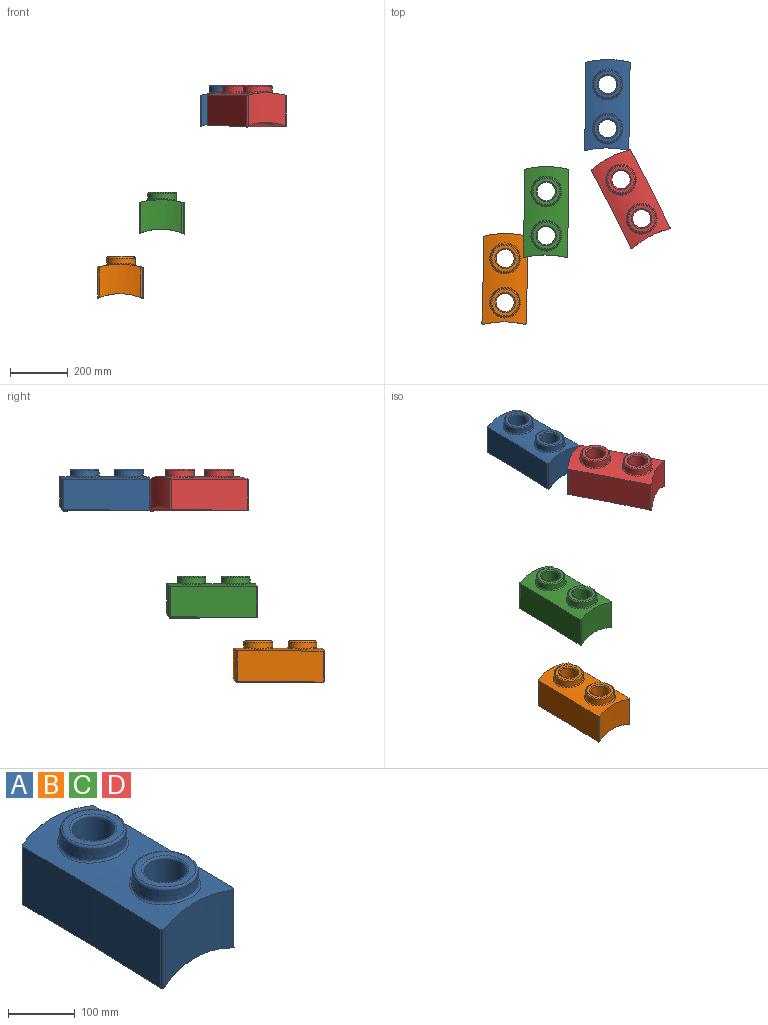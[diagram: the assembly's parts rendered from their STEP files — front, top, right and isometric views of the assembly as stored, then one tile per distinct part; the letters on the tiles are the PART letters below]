
ASSEMBLY  parts=4 mates=1
PART A: 32 faces, bbox 157.2x313.4x143.9 mm
  f0: cylinder r=304.8mm len=313.43mm, axis (0,-1,0), area 29104.2mm2, adj f2,f3,f4,f5,f16,f17,f28,f29
  f1: cylinder r=203.2mm len=313.43mm, axis (0,-1,0), area 28881.3mm2, adj f2,f3,f4,f5,f24,f25,f28,f29
  f2: cylinder r=8000mm len=297.11mm, axis (0,0,-1), area 31878.8mm2, adj f0,f1,f28,f31
  f3: cylinder r=304.8mm len=146.61mm, axis (0,0,-1), area 15275.7mm2, adj f0,f1,f28,f29
  f4: cylinder r=7847.6mm len=296.74mm, axis (0,0,-1), area 31538.3mm2, adj f0,f1,f29,f30
  f5: cylinder r=304.8mm len=143.08mm, axis (0,0,-1), area 14885.5mm2, adj f0,f1,f30,f31
  f6: cone r=50.8mm half-angle=0.5deg, axis (0,0,-1), area 6902.9mm2, adj f25,f26
  f7: plane 94.05x94.05mm, normal (0,0,-1), area 3045mm2, adj f22,f26
  f8: cone r=50.8mm half-angle=0.5deg, axis (0,0,-1), area 6902.9mm2, adj f24,f27
  f9: plane 94.05x94.05mm, normal (0,0,-1), area 3045mm2, adj f23,f27
  f10: cylinder r=31.43mm len=93.98mm, axis (0,0,-1), area 18559.7mm2, adj f21,f23
  f11: cylinder r=31.43mm len=93.98mm, axis (0,0,-1), area 18559.7mm2, adj f18,f22
  f12: cone r=50.8mm half-angle=0.5deg, axis (0,0,-1), area 6296.1mm2, adj f17,f20
  f13: plane 91.39x91.39mm, normal (0,0,1), area 2657.6mm2, adj f20,f21
  f14: cone r=50.8mm half-angle=0.5deg, axis (0,0,-1), area 6296.1mm2, adj f16,f19
  f15: plane 91.39x91.39mm, normal (0,0,1), area 2657.6mm2, adj f18,f19
  f16: bspline ~106.96x105.73mm, area 1802.5mm2, adj f0,f14
  f17: bspline ~106.96x105.73mm, area 1802.5mm2, adj f0,f12
  f18: torus R=35.24mm, axis (0,0,1), area 1234mm2, adj f11,f15
  f19: torus R=45.69mm, axis (0,0,1), area 1799.1mm2, adj f14,f15
  f20: torus R=45.69mm, axis (0,0,1), area 1799.1mm2, adj f12,f13
  f21: torus R=35.24mm, axis (0,0,1), area 1234mm2, adj f10,f13
  f22: torus R=35.24mm, axis (0,0,1), area 1234mm2, adj f7,f11
  f23: torus R=35.24mm, axis (0,0,1), area 1234mm2, adj f9,f10
  f24: bspline ~109.63x107.73mm, area 1793.9mm2, adj f1,f8
  f25: bspline ~109.63x107.73mm, area 1793.9mm2, adj f1,f6
  f26: torus R=47.02mm, axis (0,0,1), area 1848.8mm2, adj f6,f7
  f27: torus R=47.02mm, axis (0,0,1), area 1848.8mm2, adj f8,f9
  f28: cylinder r=3.81mm len=108.28mm, axis (0,0,-1), area 541.9mm2, adj f0,f1,f2,f3
  f29: cylinder r=3.81mm len=106.74mm, axis (0,0,1), area 537.1mm2, adj f0,f1,f3,f4
  f30: cylinder r=3.81mm len=107.9mm, axis (0,0,-1), area 747.4mm2, adj f0,f1,f4,f5
  f31: cylinder r=3.81mm len=107.96mm, axis (0,0,1), area 719.9mm2, adj f0,f1,f2,f5
PART B: same geometry as A
PART C: same geometry as A
PART D: same geometry as A
PLACE A t=(-116.19,-10.98,7.73)mm fixed
PLACE B t=(-470.11,-610.24,-584.67)mm
PLACE C t=(-328.11,-379.65,-361.75)mm
PLACE D rot(axis=(0,0,1),27.9deg) t=(-34.41,-330.69,7.73)mm
MATE planar A.f6 <-> D.f8  axis (0,0,1) through (-116.19,-87.18,160.13)mm
